# Revit family: Krowne_18-508L_DeckMount_Pre-Rinse_Faucet
name_source: partatom
category: Plumbing Fixtures
revit_build: Autodesk Revit 2018 (Build: 20170223_1515(x64)
units: mm (PartAtom-declared; Revit-internal decimal feet)

## family parameters
Always vertical = Yes
Cut with Voids When Loaded = No
OmniClass Number = 23.40.40.00
OmniClass Title = Food Service Equipment and Furnishings
Part Type = Normal
Room Calculation Point = No
Round Connector Dimension = Use Diameter
Shared = No
Work Plane-Based = No

## types (1)
- 18-508L
    Assembly Code = E1090300
    Cold Water Connection Height = 0"
    Cold Water Flow = 2 GPM
    Cold Water Size = 0"
    Depth = 10"
    Description = Single Hole Deck Mount Space Saver Pre-Rense (With 8” Spout)
    Foodservice Equipment Identifier = Yes
    Height = 25 1/4"
    Hot Water Connection Height = 0"
    Hot Water Flow = 2 GPM
    Hot Water Size = 0"
    Hot Water Temperature = 100 °F
    Manufacturer = Krowne Metal
    Model = 18-508L
    URL = https://krowne.com
    Weight in Pounds = 13
    Width = 7 1/4"

## geometry (parser evidence)
native form markers: Blend x4, Sweep x3
no freeform markers — native parametric forms only
